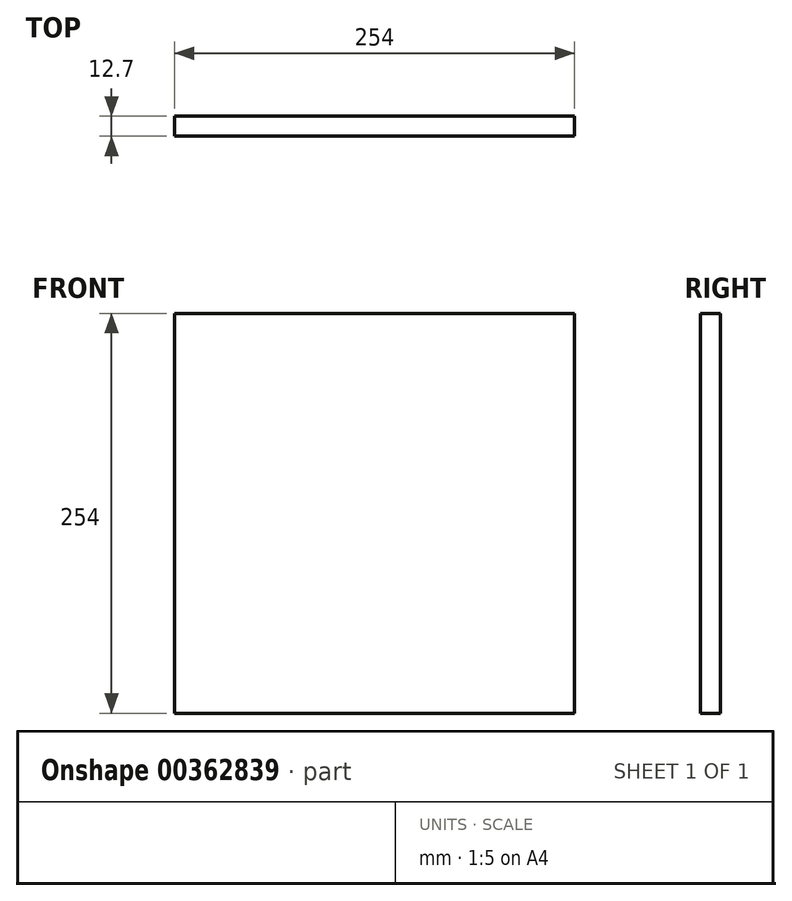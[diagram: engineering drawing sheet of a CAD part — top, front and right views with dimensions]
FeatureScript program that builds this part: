
annotation { "Feature Type Name" : "Feature", "Feature Type Description" : "" }
export const myFeature = defineFeature(function(context is Context, id is Id, definition is map)
    precondition{}
    {
        {
            var Q0;
            Q0=qCreatedBy(makeId("Front.planeOp"),FACE);
            var sketch = newSketch(context, id + "F0", { "sketchPlane" : qUnion([Q0])});
            skLineSegment(sketch, "E0.bottom", {"start": v(0, 0) * mm, "end": v(254, 0) * mm});
            skLineSegment(sketch, "E0.top", {"start": v(0, 254) * mm, "end": v(254, 254) * mm});
            skLineSegment(sketch, "E0.left", {"start": v(0, 0) * mm, "end": v(0, 254) * mm});
            skLineSegment(sketch, "E0.right", {"start": v(254, 0) * mm, "end": v(254, 254) * mm});
            skLineSegment(sketch, "E1.0", {"start": v(508, 0) * mm, "end": v(508, 117.03) * mm});
            skSolve(sketch);
        }
        {
            var Q0;
            Q0=makeQuery(id+"F0.imprint","IMPRINT",FACE,{"disambiguationData":[TD([[makeQuery(id+"F0.imprint","IMPRINT",EDGE,{"derivedFrom":sQuery(id+"F0.wireOp",EDGE,"E0.bottom")}),1.0]])]});
            extrude(context, id + "F1", {"entities" : qUnion([Q0]), "depth" : 12.7 * mm});
        }
    });
